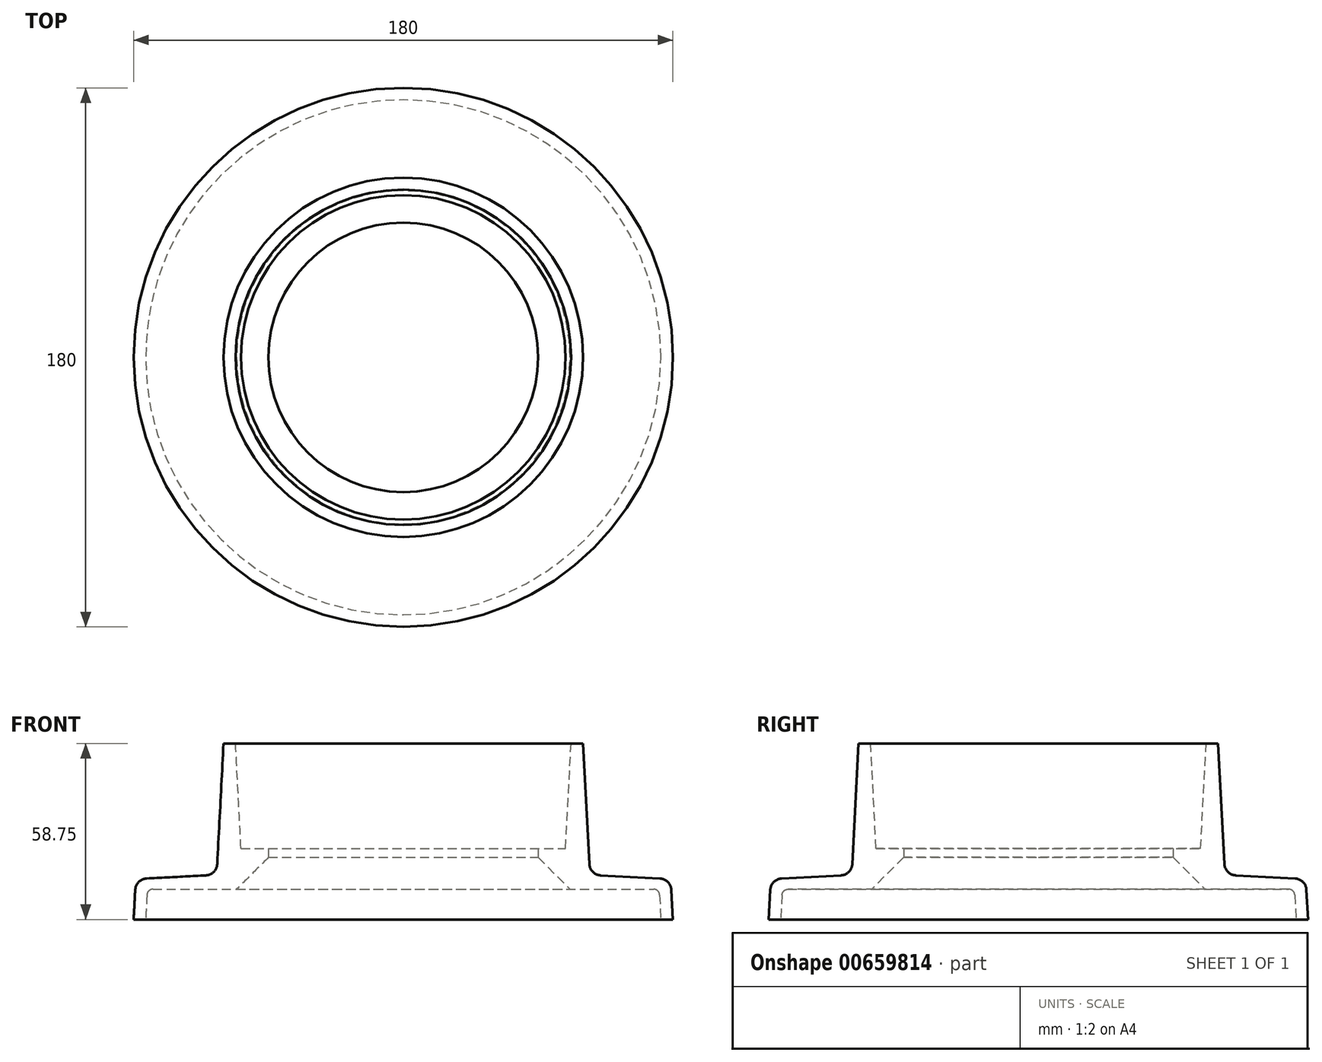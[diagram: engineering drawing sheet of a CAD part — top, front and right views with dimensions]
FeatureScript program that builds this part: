
annotation { "Feature Type Name" : "Feature", "Feature Type Description" : "" }
export const myFeature = defineFeature(function(context is Context, id is Id, definition is map)
    precondition{}
    {
        {
            var Q0;
            Q0=qCreatedBy(makeId("Front.planeOp"),FACE);
            var sketch = newSketch(context, id + "F0", { "sketchPlane" : qUnion([Q0])});
            skLineSegment(sketch, "E0", {"start": v(45, 0) * mm, "end": v(54.17, 0) * mm});
            skLineSegment(sketch, "E1", {"start": v(56, 35) * mm, "end": v(60, 35) * mm});
            skLineSegment(sketch, "E2", {"start": v(60, 35) * mm, "end": v(62.1, -5.23) * mm});
            skLineSegment(sketch, "E3", {"start": v(65.9, -9.02) * mm, "end": v(85.7, -10.06) * mm});
            skLineSegment(sketch, "E4", {"start": v(0, -4) * mm, "end": v(0, 0) * mm, "construction": true});
            skLineSegment(sketch, "E5", {"start": v(90, -23.75) * mm, "end": v(86, -23.75) * mm});
            skPoint(sketch, "E6.visualSharp", {"position": v(56, -21.06) * mm});
            skArc(sketch, "E7.filletArc", {"start": v(62.1, -5.23) * mm, "mid": v(63.27, -7.85) * mm, "end": v(65.9, -9.02) * mm});
            skPoint(sketch, "E8.visualSharp", {"position": v(95.88, -10.6) * mm});
            skLineSegment(sketch, "E9", {"start": v(45, 0) * mm, "end": v(45, -3) * mm});
            skLineSegment(sketch, "E10", {"start": v(83.57, -13.66) * mm, "end": v(55.66, -13.66) * mm});
            skPoint(sketch, "E11.visualSharp", {"position": v(96, -13.66) * mm});
            skLineSegment(sketch, "E11.filletArc", {"start": v(96, -13.66) * mm, "end": v(96, -13.66) * mm});
            skLineSegment(sketch, "E12", {"start": v(55.66, -13.66) * mm, "end": v(45, -3) * mm});
            skLineSegment(sketch, "E13", {"start": v(56, 35) * mm, "end": v(54.17, 0) * mm});
            skPoint(sketch, "E14.orphan", {"position": v(56, 0) * mm});
            skLineSegment(sketch, "E15", {"start": v(86, -23.75) * mm, "end": v(85.57, -15.55) * mm});
            skArc(sketch, "E16.filletArc", {"start": v(85.57, -15.55) * mm, "mid": v(84.95, -14.2) * mm, "end": v(83.57, -13.66) * mm});
            skLineSegment(sketch, "E17", {"start": v(90, -23.75) * mm, "end": v(89.48, -13.84) * mm});
            skArc(sketch, "E18.filletArc", {"start": v(89.48, -13.84) * mm, "mid": v(88.31, -11.22) * mm, "end": v(85.7, -10.06) * mm});
            skSolve(sketch);
        }
        {
            var Q0;
            Q0 = qSketchRegion(id + "F0", true);
            var Q1;
            Q1=sQuery(id+"F0.wireOp",EDGE,"E4");
            revolve(context, id + "F1", {"entities" : qUnion([Q0]), "axis" : qUnion([Q1]), "revolveType" : RevolveType.FULL});
        }
    });
